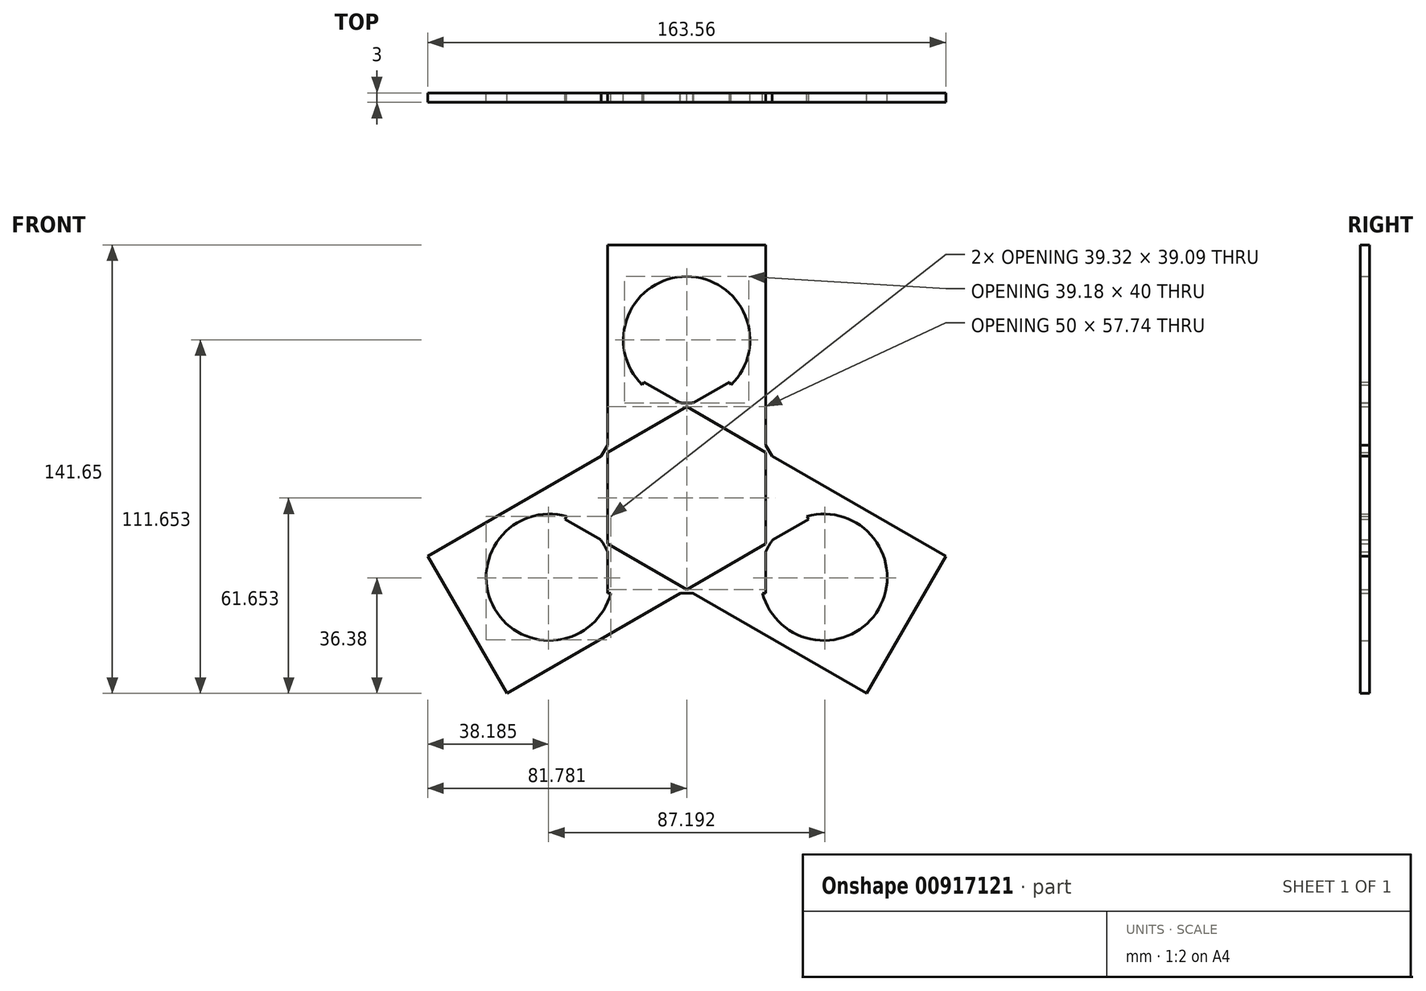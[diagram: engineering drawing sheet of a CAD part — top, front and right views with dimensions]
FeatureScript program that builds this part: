
annotation { "Feature Type Name" : "Feature", "Feature Type Description" : "" }
export const myFeature = defineFeature(function(context is Context, id is Id, definition is map)
    precondition{}
    {
        {
            var Q0;
            Q0=qCreatedBy(makeId("Front.planeOp"),FACE);
            var sketch = newSketch(context, id + "F0", { "sketchPlane" : qUnion([Q0])});
            skCircle(sketch, "E0", {"center": v(-41.45, -33.92) * mm, "radius": 20 * mm});
            skCircle(sketch, "E1", {"center": v(-41.45, 16.08) * mm, "radius": 20 * mm});
            skLineSegment(sketch, "E2.bottom", {"start": v(-66.45, 46.08) * mm, "end": v(-16.45, 46.08) * mm});
            skLineSegment(sketch, "E2.top", {"start": v(-66.45, -63.92) * mm, "end": v(-16.45, -63.92) * mm});
            skLineSegment(sketch, "E2.left", {"start": v(-66.45, 46.08) * mm, "end": v(-66.45, -63.92) * mm});
            skLineSegment(sketch, "E2.right", {"start": v(-16.45, 46.08) * mm, "end": v(-16.45, -63.92) * mm});
            skLineSegment(sketch, "E3.1.1", {"start": v(-98.23, -95.57) * mm, "end": v(-123.23, -52.27) * mm});
            skCircle(sketch, "E3.1.2", {"center": v(-84.75, -58.92) * mm, "radius": 20 * mm});
            skLineSegment(sketch, "E3.1.3", {"start": v(-98.23, -95.57) * mm, "end": v(-2.97, -40.57) * mm});
            skLineSegment(sketch, "E3.1.4", {"start": v(-123.23, -52.27) * mm, "end": v(-27.97, 2.73) * mm});
            skLineSegment(sketch, "E3.1.5", {"start": v(-2.97, -40.57) * mm, "end": v(-27.97, 2.73) * mm});
            skLineSegment(sketch, "E3.2.1", {"start": v(40.33, -52.27) * mm, "end": v(15.33, -95.57) * mm});
            skCircle(sketch, "E3.2.2", {"center": v(1.85, -58.92) * mm, "radius": 20 * mm});
            skLineSegment(sketch, "E3.2.3", {"start": v(40.33, -52.27) * mm, "end": v(-54.93, 2.73) * mm});
            skLineSegment(sketch, "E3.2.4", {"start": v(15.33, -95.57) * mm, "end": v(-79.93, -40.57) * mm});
            skLineSegment(sketch, "E3.2.5", {"start": v(-54.93, 2.73) * mm, "end": v(-79.93, -40.57) * mm});
            skSolve(sketch);
        }
        {
            var Q0;
            {var subQ0=sQuery(id+"F0.wireOp",EDGE,"E3.1.4");var subQ1=sQuery(id+"F0.wireOp",EDGE,"E1");var subQ2=makeQuery(id+"F0.imprint","INTERSECT",VERTEX,{"derivedFrom":[subQ1,subQ0]});Q0=makeQuery(id+"F0.imprint","IMPRINT",FACE,{"disambiguationData":[TD([[makeQuery(id+"F0.imprint","IMPRINT",EDGE,{"disambiguationData":[TD([[subQ2,-1.0]])],"derivedFrom":subQ1}),1.0]])]});}
            var Q1;
            {var subQ0=sQuery(id+"F0.wireOp",EDGE,"E3.1.5");var subQ1=sQuery(id+"F0.wireOp",EDGE,"E3.1.3");var subQ2=makeQuery(id+"F0.imprint","INTERSECT",VERTEX,{"derivedFrom":[subQ1,subQ0]});Q1=makeQuery(id+"F0.imprint","IMPRINT",FACE,{"disambiguationData":[TD([[makeQuery(id+"F0.imprint","IMPRINT",EDGE,{"disambiguationData":[TD([[subQ2,1.0]])],"derivedFrom":subQ1}),1.0]])]});}
            var Q2;
            {var subQ3=sQuery(id+"F0.wireOp",EDGE,"E1");var subQ7=sQuery(id+"F0.wireOp",EDGE,"E3.1.4");var subQ8=makeQuery(id+"F0.imprint","INTERSECT",VERTEX,{"derivedFrom":[subQ3,subQ7]});Q2=makeQuery(id+"F0.imprint","IMPRINT",FACE,{"disambiguationData":[TD([[makeQuery(id+"F0.imprint","IMPRINT",EDGE,{"disambiguationData":[TD([[subQ8,-1.0]])],"derivedFrom":subQ3}),-1.0]])]});}
            var Q3;
            {var subQ1=sQuery(id+"F0.wireOp",EDGE,"E2.top");var subQ7=sQuery(id+"F0.wireOp",EDGE,"E3.2.4");var subQ9=makeQuery(id+"F0.imprint","INTERSECT",VERTEX,{"derivedFrom":[subQ1,subQ7]});Q3=makeQuery(id+"F0.imprint","IMPRINT",FACE,{"disambiguationData":[TD([[makeQuery(id+"F0.imprint","IMPRINT",EDGE,{"disambiguationData":[TD([[subQ9,-1.0]])],"derivedFrom":subQ1}),1.0]])]});}
            var Q4;
            {var subQ0=sQuery(id+"F0.wireOp",EDGE,"E3.1.3");var subQ1=sQuery(id+"F0.wireOp",EDGE,"E2.right");var subQ2=makeQuery(id+"F0.imprint","INTERSECT",VERTEX,{"derivedFrom":[subQ1,subQ0]});Q4=makeQuery(id+"F0.imprint","IMPRINT",FACE,{"disambiguationData":[TD([[makeQuery(id+"F0.imprint","IMPRINT",EDGE,{"disambiguationData":[TD([[subQ2,-1.0]])],"derivedFrom":subQ1}),1.0]])]});}
            var Q5;
            {var subQ0=sQuery(id+"F0.wireOp",EDGE,"E3.2.3");var subQ5=sQuery(id+"F0.wireOp",EDGE,"E2.right");var subQ6=makeQuery(id+"F0.imprint","INTERSECT",VERTEX,{"derivedFrom":[subQ5,subQ0]});Q5=makeQuery(id+"F0.imprint","IMPRINT",FACE,{"disambiguationData":[TD([[makeQuery(id+"F0.imprint","IMPRINT",EDGE,{"disambiguationData":[TD([[subQ6,-1.0]])],"derivedFrom":subQ5}),1.0]])]});}
            var Q6;
            {var subQ0=sQuery(id+"F0.wireOp",EDGE,"E2.right");var subQ1=sQuery(id+"F0.wireOp",EDGE,"E2.top");var subQ2=makeQuery(id+"F0.imprint","INTERSECT",VERTEX,{"derivedFrom":[subQ1,subQ0]});Q6=makeQuery(id+"F0.imprint","IMPRINT",FACE,{"disambiguationData":[TD([[makeQuery(id+"F0.imprint","IMPRINT",EDGE,{"disambiguationData":[TD([[subQ2,1.0]])],"derivedFrom":subQ1}),1.0]])]});}
            var Q7;
            {var subQ0=sQuery(id+"F0.wireOp",EDGE,"E3.1.5");var subQ1=sQuery(id+"F0.wireOp",EDGE,"E2.right");var subQ2=makeQuery(id+"F0.imprint","INTERSECT",VERTEX,{"derivedFrom":[subQ1,subQ0]});Q7=makeQuery(id+"F0.imprint","IMPRINT",FACE,{"disambiguationData":[TD([[makeQuery(id+"F0.imprint","IMPRINT",EDGE,{"disambiguationData":[TD([[subQ2,-1.0]])],"derivedFrom":subQ1}),1.0]])]});}
            var Q8;
            {var subQ1=sQuery(id+"F0.wireOp",EDGE,"E2.bottom");Q8=makeQuery(id+"F0.imprint","IMPRINT",FACE,{"disambiguationData":[TD([[makeQuery(id+"F0.imprint","IMPRINT",EDGE,{"derivedFrom":subQ1}),-1.0]])]});}
            var Q9;
            {var subQ6=sQuery(id+"F0.wireOp",EDGE,"E3.1.1");Q9=makeQuery(id+"F0.imprint","IMPRINT",FACE,{"disambiguationData":[TD([[makeQuery(id+"F0.imprint","IMPRINT",EDGE,{"derivedFrom":subQ6}),-1.0]])]});}
            var Q10;
            {var subQ5=sQuery(id+"F0.wireOp",EDGE,"E3.2.1");Q10=makeQuery(id+"F0.imprint","IMPRINT",FACE,{"disambiguationData":[TD([[makeQuery(id+"F0.imprint","IMPRINT",EDGE,{"derivedFrom":subQ5}),-1.0]])]});}
            var Q11;
            {var subQ5=sQuery(id+"F0.wireOp",EDGE,"E3.1.3");var subQ6=sQuery(id+"F0.wireOp",EDGE,"E2.top");var subQ7=makeQuery(id+"F0.imprint","INTERSECT",VERTEX,{"derivedFrom":[subQ6,subQ5]});Q11=makeQuery(id+"F0.imprint","IMPRINT",FACE,{"disambiguationData":[TD([[makeQuery(id+"F0.imprint","IMPRINT",EDGE,{"disambiguationData":[TD([[subQ7,1.0]])],"derivedFrom":subQ6}),1.0]])]});}
            var Q12;
            {var subQ1=sQuery(id+"F0.wireOp",EDGE,"E2.left");var subQ6=sQuery(id+"F0.wireOp",EDGE,"E3.1.4");var subQ8=makeQuery(id+"F0.imprint","INTERSECT",VERTEX,{"derivedFrom":[subQ1,subQ6]});Q12=makeQuery(id+"F0.imprint","IMPRINT",FACE,{"disambiguationData":[TD([[makeQuery(id+"F0.imprint","IMPRINT",EDGE,{"disambiguationData":[TD([[subQ8,-1.0]])],"derivedFrom":subQ1}),-1.0]])]});}
            var Q13;
            {var subQ0=sQuery(id+"F0.wireOp",EDGE,"E3.2.3");var subQ1=sQuery(id+"F0.wireOp",EDGE,"E1");var subQ2=makeQuery(id+"F0.imprint","INTERSECT",VERTEX,{"derivedFrom":[subQ1,subQ0]});Q13=makeQuery(id+"F0.imprint","IMPRINT",FACE,{"disambiguationData":[TD([[makeQuery(id+"F0.imprint","IMPRINT",EDGE,{"disambiguationData":[TD([[subQ2,1.0]])],"derivedFrom":subQ1}),-1.0]])]});}
            var Q14;
            Q14=makeQuery(id+"F0.imprint","IMPRINT",FACE,{"disambiguationData":[TD([[makeQuery(id+"F0.imprint","IMPRINT",EDGE,{"derivedFrom":sQuery(id+"F0.wireOp",EDGE,"E0")}),-1.0]])]});
            var Q15;
            {var subQ0=sQuery(id+"F0.wireOp",EDGE,"E2.left");var subQ1=sQuery(id+"F0.wireOp",EDGE,"E2.top");var subQ2=makeQuery(id+"F0.imprint","INTERSECT",VERTEX,{"derivedFrom":[subQ1,subQ0]});Q15=makeQuery(id+"F0.imprint","IMPRINT",FACE,{"disambiguationData":[TD([[makeQuery(id+"F0.imprint","IMPRINT",EDGE,{"disambiguationData":[TD([[subQ2,-1.0]])],"derivedFrom":subQ1}),1.0]])]});}
            var Q16;
            {var subQ0=sQuery(id+"F0.wireOp",EDGE,"E3.1.3");var subQ1=sQuery(id+"F0.wireOp",EDGE,"E2.top");var subQ2=makeQuery(id+"F0.imprint","INTERSECT",VERTEX,{"derivedFrom":[subQ1,subQ0]});Q16=makeQuery(id+"F0.imprint","IMPRINT",FACE,{"disambiguationData":[TD([[makeQuery(id+"F0.imprint","IMPRINT",EDGE,{"disambiguationData":[TD([[subQ2,-1.0]])],"derivedFrom":subQ1}),1.0]])]});}
            var Q17;
            {var subQ0=sQuery(id+"F0.wireOp",EDGE,"E3.2.5");var subQ1=sQuery(id+"F0.wireOp",EDGE,"E2.left");var subQ2=makeQuery(id+"F0.imprint","INTERSECT",VERTEX,{"derivedFrom":[subQ1,subQ0]});Q17=makeQuery(id+"F0.imprint","IMPRINT",FACE,{"disambiguationData":[TD([[makeQuery(id+"F0.imprint","IMPRINT",EDGE,{"disambiguationData":[TD([[subQ2,-1.0]])],"derivedFrom":subQ1}),-1.0]])]});}
            var Q18;
            {var subQ0=sQuery(id+"F0.wireOp",EDGE,"E3.2.4");var subQ1=sQuery(id+"F0.wireOp",EDGE,"E3.1.2");var subQ2=makeQuery(id+"F0.imprint","INTERSECT",VERTEX,{"derivedFrom":[subQ1,subQ0]});Q18=makeQuery(id+"F0.imprint","IMPRINT",FACE,{"disambiguationData":[TD([[makeQuery(id+"F0.imprint","IMPRINT",EDGE,{"disambiguationData":[TD([[subQ2,-1.0]])],"derivedFrom":subQ1}),1.0]])]});}
            var Q19;
            {var subQ0=sQuery(id+"F0.wireOp",EDGE,"E3.2.3");var subQ1=sQuery(id+"F0.wireOp",EDGE,"E1");var subQ2=makeQuery(id+"F0.imprint","INTERSECT",VERTEX,{"derivedFrom":[subQ1,subQ0]});Q19=makeQuery(id+"F0.imprint","IMPRINT",FACE,{"disambiguationData":[TD([[makeQuery(id+"F0.imprint","IMPRINT",EDGE,{"disambiguationData":[TD([[subQ2,-1.0]])],"derivedFrom":subQ1}),-1.0]])]});}
            var Q20;
            {var subQ0=sQuery(id+"F0.wireOp",EDGE,"E3.2.4");var subQ1=sQuery(id+"F0.wireOp",EDGE,"E2.left");var subQ2=makeQuery(id+"F0.imprint","INTERSECT",VERTEX,{"derivedFrom":[subQ1,subQ0]});Q20=makeQuery(id+"F0.imprint","IMPRINT",FACE,{"disambiguationData":[TD([[makeQuery(id+"F0.imprint","IMPRINT",EDGE,{"disambiguationData":[TD([[subQ2,-1.0]])],"derivedFrom":subQ1}),-1.0]])]});}
            var Q21;
            {var subQ0=sQuery(id+"F0.wireOp",EDGE,"E3.2.3");var subQ1=sQuery(id+"F0.wireOp",EDGE,"E1");var subQ2=makeQuery(id+"F0.imprint","INTERSECT",VERTEX,{"derivedFrom":[subQ1,subQ0]});Q21=makeQuery(id+"F0.imprint","IMPRINT",FACE,{"disambiguationData":[TD([[makeQuery(id+"F0.imprint","IMPRINT",EDGE,{"disambiguationData":[TD([[subQ2,1.0]])],"derivedFrom":subQ1}),1.0]])]});}
            extrude(context, id + "F1", {"entities" : qUnion([Q0, Q1, Q2, Q3, Q4, Q5, Q6, Q7, Q8, Q9, Q10, Q11, Q12, Q13, Q14, Q15, Q16, Q17, Q18, Q19, Q20, Q21]), "depth" : 3 * mm, "offsetDistance" : 25 * mm});
        }
    });
